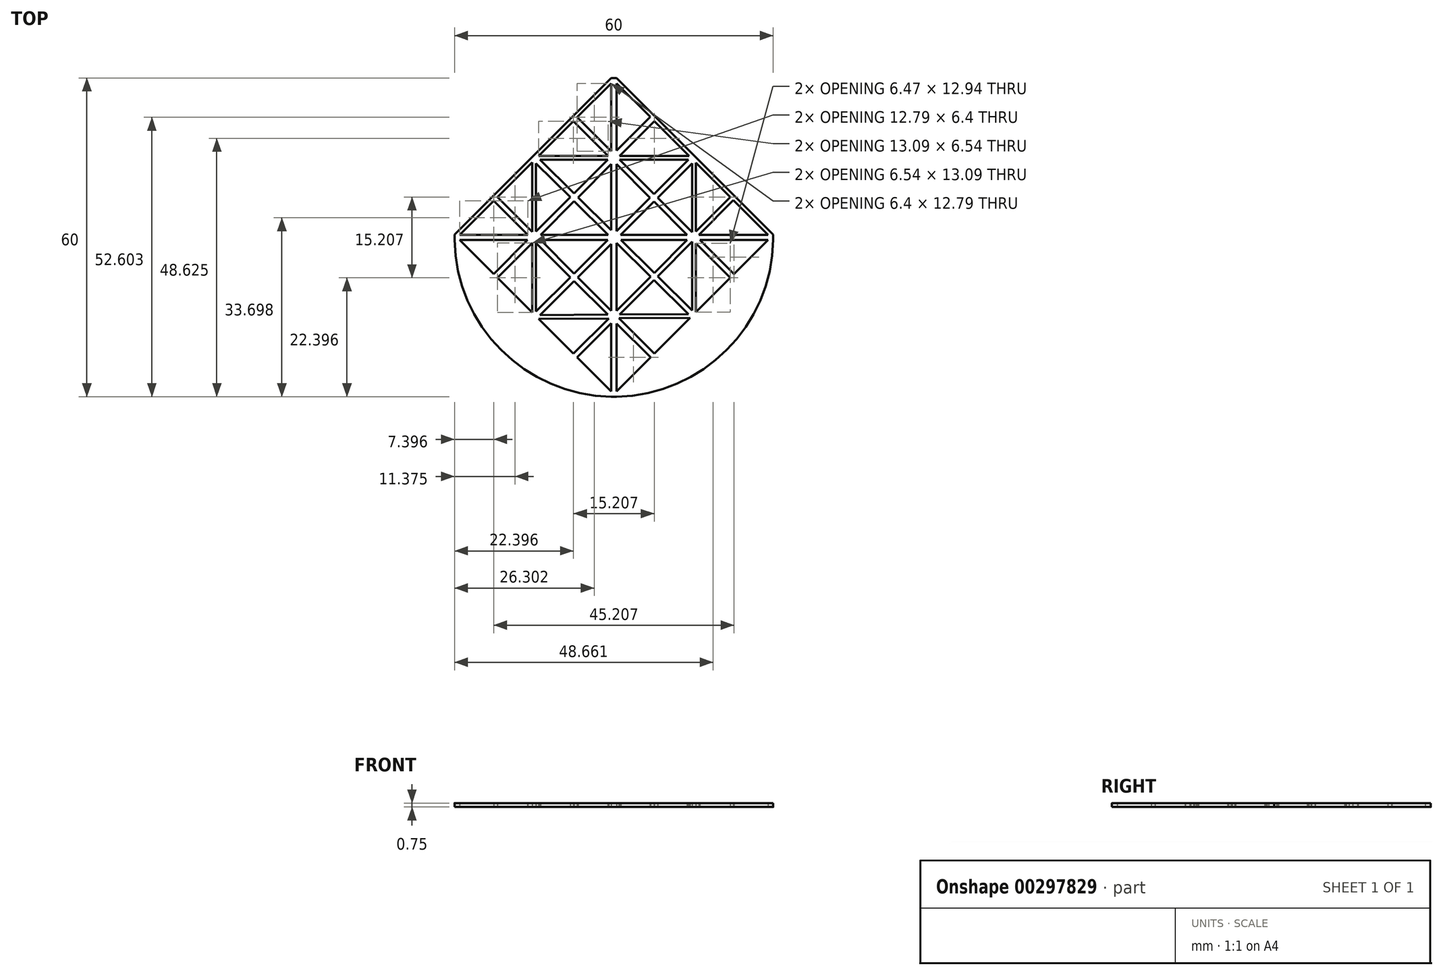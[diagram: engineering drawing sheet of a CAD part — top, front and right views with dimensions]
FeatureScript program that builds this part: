
annotation { "Feature Type Name" : "Feature", "Feature Type Description" : "" }
export const myFeature = defineFeature(function(context is Context, id is Id, definition is map)
    precondition{}
    {
        {
            var Q0;
            Q0=qCreatedBy(makeId("Top.planeOp"),FACE);
            var sketch = newSketch(context, id + "F0", { "sketchPlane" : qUnion([Q0])});
            skCircle(sketch, "E0", {"center": v(0, 0) * mm, "radius": 30 * mm});
            skLineSegment(sketch, "E1", {"start": v(-30, 0.5) * mm, "end": v(-0.5, 30) * mm});
            skLineSegment(sketch, "E2", {"start": v(0.5, 30) * mm, "end": v(30, 0.5) * mm});
            skLineSegment(sketch, "E3", {"start": v(30, 0.5) * mm, "end": v(30, -0.5) * mm});
            skLineSegment(sketch, "E4", {"start": v(-30, 0.5) * mm, "end": v(-30, 0.5) * mm});
            skLineSegment(sketch, "E5", {"start": v(-30, -0.5) * mm, "end": v(-0.5, -30) * mm});
            skLineSegment(sketch, "E6", {"start": v(0.5, -30) * mm, "end": v(30, -0.5) * mm});
            skLineSegment(sketch, "E7", {"start": v(30, 0.5) * mm, "end": v(30, 0.5) * mm});
            skLineSegment(sketch, "E8", {"start": v(30, -0.5) * mm, "end": v(30, -0.5) * mm});
            skLineSegment(sketch, "E9", {"start": v(0.5, 30) * mm, "end": v(0.5, 30) * mm});
            skLineSegment(sketch, "E10", {"start": v(-15.35, -14.15) * mm, "end": v(-15.35, -1.06) * mm});
            skLineSegment(sketch, "E11", {"start": v(-14.15, 15.35) * mm, "end": v(-1.06, 15.35) * mm});
            skLineSegment(sketch, "E12", {"start": v(15.43, 14.07) * mm, "end": v(15.43, 1.13) * mm});
            skLineSegment(sketch, "E13", {"start": v(14.36, -15.14) * mm, "end": v(0.95, -15.24) * mm});
            skLineSegment(sketch, "E14", {"start": v(-0.5, 30) * mm, "end": v(-0.5, 30) * mm});
            skLineSegment(sketch, "E15", {"start": v(-14.65, -13.94) * mm, "end": v(-8.2, -7.5) * mm});
            skLineSegment(sketch, "E16", {"start": v(14.72, -13.73) * mm, "end": v(8.24, -7.32) * mm});
            skLineSegment(sketch, "E17", {"start": v(-14.65, 13.95) * mm, "end": v(-8.2, 7.57) * mm});
            skLineSegment(sketch, "E18", {"start": v(7.6, 21.9) * mm, "end": v(1.06, 15.35) * mm});
            skLineSegment(sketch, "E19", {"start": v(-22.6, -6.9) * mm, "end": v(-16.24, -0.5) * mm});
            skLineSegment(sketch, "E20", {"start": v(22.46, 7.04) * mm, "end": v(15.99, 0.5) * mm});
            skLineSegment(sketch, "E21", {"start": v(-7.6, -21.9) * mm, "end": v(-0.96, -15.25) * mm});
            skLineSegment(sketch, "E22", {"start": v(7.6, -21.9) * mm, "end": v(0.95, -15.24) * mm});
            skLineSegment(sketch, "E23", {"start": v(-22.6, 6.9) * mm, "end": v(-16.2, 0.5) * mm});
            skLineSegment(sketch, "E24", {"start": v(22.78, -7.07) * mm, "end": v(16.2, -0.5) * mm});
            skLineSegment(sketch, "E25", {"start": v(-7.6, 21.9) * mm, "end": v(-1.06, 15.35) * mm});
            skLineSegment(sketch, "E26.trimOffspring", {"start": v(-15.35, 14.15) * mm, "end": v(-21.9, 7.6) * mm});
            skLineSegment(sketch, "E27.trimOffspring", {"start": v(-14.65, 13.95) * mm, "end": v(-14.65, 1.1) * mm});
            skLineSegment(sketch, "E28.trimOffspring", {"start": v(-7.6, 21.9) * mm, "end": v(-14.15, 15.35) * mm});
            skLineSegment(sketch, "E29.trimOffspring", {"start": v(-0.5, 29) * mm, "end": v(-0.5, 16.2) * mm});
            skLineSegment(sketch, "E30.trimOffspring", {"start": v(-0.5, 29) * mm, "end": v(-6.9, 22.6) * mm});
            skLineSegment(sketch, "E31.trimOffspring", {"start": v(0.5, 29) * mm, "end": v(0.5, 16.32) * mm});
            skLineSegment(sketch, "E32.trimOffspring", {"start": v(6.83, 22.67) * mm, "end": v(0.5, 29) * mm});
            skLineSegment(sketch, "E33.trimOffspring", {"start": v(0.5, 16.32) * mm, "end": v(6.83, 22.67) * mm});
            skLineSegment(sketch, "E34.trimOffspring", {"start": v(-0.5, 16.2) * mm, "end": v(-6.9, 22.6) * mm});
            skLineSegment(sketch, "E35.trimOffspring", {"start": v(-1.16, 14.65) * mm, "end": v(-13.93, 14.65) * mm});
            skLineSegment(sketch, "E36.trimOffspring", {"start": v(-0.5, 13.8) * mm, "end": v(-0.5, 1.34) * mm});
            skLineSegment(sketch, "E37.trimOffspring", {"start": v(0.5, 13.8) * mm, "end": v(6.82, 7.47) * mm});
            skLineSegment(sketch, "E38.trimOffspring", {"start": v(-0.5, 13.8) * mm, "end": v(-6.76, 7.54) * mm});
            skLineSegment(sketch, "E39.trimOffspring", {"start": v(-22.6, 6.9) * mm, "end": v(-29, 0.5) * mm});
            skLineSegment(sketch, "E40.trimOffspring", {"start": v(-29, -0.5) * mm, "end": v(-22.6, -6.9) * mm});
            skLineSegment(sketch, "E41.trimOffspring", {"start": v(-30, -0.5) * mm, "end": v(-30, -0.5) * mm});
            skLineSegment(sketch, "E42.trimOffspring", {"start": v(-29, 0.5) * mm, "end": v(-16.2, 0.5) * mm});
            skLineSegment(sketch, "E43.trimOffspring", {"start": v(-21.9, -7.6) * mm, "end": v(-15.35, -14.15) * mm});
            skLineSegment(sketch, "E44.trimOffspring", {"start": v(-14.15, -15.35) * mm, "end": v(-7.6, -21.9) * mm});
            skLineSegment(sketch, "E45.trimOffspring", {"start": v(-13.93, -14.64) * mm, "end": v(-1.16, -14.55) * mm});
            skLineSegment(sketch, "E46.trimOffspring", {"start": v(-6.9, -22.6) * mm, "end": v(-0.5, -29) * mm});
            skLineSegment(sketch, "E47.trimOffspring", {"start": v(-0.5, -30) * mm, "end": v(-0.5, -30) * mm});
            skLineSegment(sketch, "E48.trimOffspring", {"start": v(0.5, -30) * mm, "end": v(0.5, -30) * mm});
            skLineSegment(sketch, "E49.trimOffspring", {"start": v(6.9, -22.6) * mm, "end": v(0.5, -29) * mm});
            skLineSegment(sketch, "E50.trimOffspring", {"start": v(14.72, -13.73) * mm, "end": v(14.72, -0.78) * mm});
            skLineSegment(sketch, "E51.trimOffspring", {"start": v(14.36, -15.14) * mm, "end": v(7.6, -21.9) * mm});
            skLineSegment(sketch, "E52.trimOffspring", {"start": v(-7.46, 6.83) * mm, "end": v(-1.07, 0.5) * mm});
            skLineSegment(sketch, "E53.trimOffspring", {"start": v(-7.5, 8.28) * mm, "end": v(-1.16, 14.65) * mm});
            skLineSegment(sketch, "E54.trimOffspring", {"start": v(-7.5, 8.28) * mm, "end": v(-13.93, 14.65) * mm});
            skLineSegment(sketch, "E55.trimOffspring", {"start": v(-7.46, 6.83) * mm, "end": v(-13.8, 0.5) * mm});
            skLineSegment(sketch, "E56.trimOffspring", {"start": v(-1.17, -0.5) * mm, "end": v(-13.8, -0.5) * mm});
            skLineSegment(sketch, "E57.trimOffspring", {"start": v(-0.5, -1.24) * mm, "end": v(-0.5, -13.8) * mm});
            skLineSegment(sketch, "E58.trimOffspring", {"start": v(-0.5, 1.34) * mm, "end": v(-6.76, 7.54) * mm});
            skLineSegment(sketch, "E59.trimOffspring", {"start": v(0.5, 1.17) * mm, "end": v(6.82, 7.47) * mm});
            skLineSegment(sketch, "E60.trimOffspring", {"start": v(1.24, 0.5) * mm, "end": v(13.8, 0.5) * mm});
            skLineSegment(sketch, "E61.trimOffspring", {"start": v(0.5, -1.06) * mm, "end": v(0.5, -13.8) * mm});
            skLineSegment(sketch, "E62.trimOffspring", {"start": v(-0.5, -1.24) * mm, "end": v(-6.78, -7.5) * mm});
            skLineSegment(sketch, "E63.trimOffspring", {"start": v(0.5, -1.06) * mm, "end": v(6.9, -7.4) * mm});
            skLineSegment(sketch, "E64.trimOffspring", {"start": v(1.06, 15.35) * mm, "end": v(14.15, 15.35) * mm});
            skLineSegment(sketch, "E65.trimOffspring", {"start": v(7.53, 8.18) * mm, "end": v(14, 14.65) * mm});
            skLineSegment(sketch, "E66.trimOffspring", {"start": v(7.53, 6.77) * mm, "end": v(1.24, 0.5) * mm});
            skLineSegment(sketch, "E67.trimOffspring", {"start": v(7.53, 6.77) * mm, "end": v(13.8, 0.5) * mm});
            skLineSegment(sketch, "E68.trimOffspring", {"start": v(14.15, 15.35) * mm, "end": v(7.6, 21.9) * mm});
            skLineSegment(sketch, "E69.trimOffspring", {"start": v(14, 14.65) * mm, "end": v(1.06, 14.65) * mm});
            skLineSegment(sketch, "E70.trimOffspring", {"start": v(14.72, 13.94) * mm, "end": v(8.23, 7.47) * mm});
            skLineSegment(sketch, "E71.trimOffspring", {"start": v(21.9, 7.6) * mm, "end": v(15.43, 14.07) * mm});
            skLineSegment(sketch, "E72.trimOffspring", {"start": v(29, 0.5) * mm, "end": v(22.46, 7.04) * mm});
            skLineSegment(sketch, "E73.trimOffspring", {"start": v(29, -0.5) * mm, "end": v(15.43, -14.07) * mm});
            skLineSegment(sketch, "E74.trimOffspring", {"start": v(29, -0.5) * mm, "end": v(16.2, -0.5) * mm});
            skLineSegment(sketch, "E75.trimOffspring", {"start": v(14.72, 1) * mm, "end": v(14.72, 13.94) * mm});
            skLineSegment(sketch, "E76.trimOffspring", {"start": v(14.72, 1) * mm, "end": v(1.06, 14.65) * mm});
            skLineSegment(sketch, "E77.trimOffspring", {"start": v(15.43, 1.13) * mm, "end": v(21.9, 7.6) * mm});
            skLineSegment(sketch, "E78.trimOffspring", {"start": v(14.72, -0.78) * mm, "end": v(8.24, -7.32) * mm});
            skLineSegment(sketch, "E79.trimOffspring", {"start": v(15.43, -1.13) * mm, "end": v(22.07, -7.78) * mm});
            skLineSegment(sketch, "E80.trimOffspring", {"start": v(15.43, -1.13) * mm, "end": v(15.43, -14.07) * mm});
            skLineSegment(sketch, "E81.trimOffspring", {"start": v(15.99, 0.5) * mm, "end": v(29, 0.5) * mm});
            skLineSegment(sketch, "E82.trimOffspring", {"start": v(13.8, -0.5) * mm, "end": v(1.36, -0.5) * mm});
            skLineSegment(sketch, "E83.trimOffspring", {"start": v(-0.96, -15.25) * mm, "end": v(-14.15, -15.35) * mm});
            skLineSegment(sketch, "E84.trimOffspring", {"start": v(-0.5, -16.14) * mm, "end": v(-0.5, -29) * mm});
            skLineSegment(sketch, "E85.trimOffspring", {"start": v(-0.5, -16.14) * mm, "end": v(-6.9, -22.6) * mm});
            skLineSegment(sketch, "E86.trimOffspring", {"start": v(0.5, -16.2) * mm, "end": v(6.9, -22.6) * mm});
            skLineSegment(sketch, "E87.trimOffspring", {"start": v(0.5, -16.2) * mm, "end": v(0.5, -29) * mm});
            skLineSegment(sketch, "E88.trimOffspring", {"start": v(1.1, -14.53) * mm, "end": v(14.01, -14.44) * mm});
            skLineSegment(sketch, "E89.trimOffspring", {"start": v(0.5, -13.8) * mm, "end": v(6.9, -7.4) * mm});
            skLineSegment(sketch, "E90.trimOffspring", {"start": v(-0.5, -13.8) * mm, "end": v(-6.78, -7.5) * mm});
            skLineSegment(sketch, "E91.trimOffspring", {"start": v(-7.5, -6.8) * mm, "end": v(-13.8, -0.5) * mm});
            skLineSegment(sketch, "E92.trimOffspring", {"start": v(-7.5, -6.8) * mm, "end": v(-1.17, -0.5) * mm});
            skLineSegment(sketch, "E93.trimOffspring", {"start": v(-7.5, -8.22) * mm, "end": v(-1.16, -14.55) * mm});
            skLineSegment(sketch, "E94.trimOffspring", {"start": v(-7.5, -8.22) * mm, "end": v(-13.93, -14.64) * mm});
            skLineSegment(sketch, "E95.trimOffspring", {"start": v(-16.24, -0.5) * mm, "end": v(-29, -0.5) * mm});
            skLineSegment(sketch, "E96.trimOffspring", {"start": v(-15.35, -1.06) * mm, "end": v(-21.9, -7.6) * mm});
            skLineSegment(sketch, "E97.trimOffspring", {"start": v(-14.65, -1.06) * mm, "end": v(-14.65, -13.94) * mm});
            skLineSegment(sketch, "E98.trimOffspring", {"start": v(-13.8, 0.5) * mm, "end": v(-1.07, 0.5) * mm});
            skLineSegment(sketch, "E99.trimOffspring", {"start": v(-14.65, 1.1) * mm, "end": v(-8.2, 7.57) * mm});
            skLineSegment(sketch, "E100.trimOffspring", {"start": v(-15.35, 1.06) * mm, "end": v(-21.9, 7.6) * mm});
            skLineSegment(sketch, "E101.trimOffspring", {"start": v(-15.35, 1.06) * mm, "end": v(-15.35, 14.15) * mm});
            skLineSegment(sketch, "E102.trimOffspring", {"start": v(-14.65, -1.06) * mm, "end": v(-8.2, -7.5) * mm});
            skLineSegment(sketch, "E103", {"start": v(0.5, 13.8) * mm, "end": v(0.5, 1.17) * mm});
            skLineSegment(sketch, "E104.trimOffspring", {"start": v(7.6, -6.69) * mm, "end": v(13.8, -0.5) * mm});
            skLineSegment(sketch, "E105.trimOffspring", {"start": v(7.6, -6.69) * mm, "end": v(1.36, -0.5) * mm});
            skLineSegment(sketch, "E106.trimOffspring", {"start": v(7.54, -8.03) * mm, "end": v(1.1, -14.53) * mm});
            skLineSegment(sketch, "E107.trimOffspring", {"start": v(7.54, -8.03) * mm, "end": v(14.01, -14.44) * mm});
            skSolve(sketch);
        }
        {
            var Q0;
            Q0=makeQuery(id+"F0.imprint","IMPRINT",FACE,{"disambiguationData":[TD([[makeQuery(id+"F0.imprint","IMPRINT",EDGE,{"derivedFrom":sQuery(id+"F0.wireOp",EDGE,"E10")}),-1.0]])]});
            extrude(context, id + "F1", {"entities" : qUnion([Q0]), "depth" : 0.5 * mm});
        }
        {
            var Q0;
            {var subQ0=sQuery(id+"F0.wireOp",EDGE,"E6");var subQ1=sQuery(id+"F0.wireOp",EDGE,"E0");var subQ2=makeQuery(id+"F0.imprint","INTERSECT",VERTEX,{"disambiguationData":[OD(0.0)],"derivedFrom":[subQ1,subQ0]});Q0=makeQuery(id+"F0.imprint","IMPRINT",FACE,{"disambiguationData":[TD([[makeQuery(id+"F0.imprint","IMPRINT",EDGE,{"disambiguationData":[TD([[subQ2,-1.0]])],"derivedFrom":subQ1}),1.0]])]});}
            var Q1;
            {var subQ0=sQuery(id+"F0.wireOp",EDGE,"E2");var subQ1=sQuery(id+"F0.wireOp",EDGE,"E0");var subQ2=makeQuery(id+"F0.imprint","INTERSECT",VERTEX,{"disambiguationData":[OD(0.0)],"derivedFrom":[subQ1,subQ0]});Q1=makeQuery(id+"F0.imprint","IMPRINT",FACE,{"disambiguationData":[TD([[makeQuery(id+"F0.imprint","IMPRINT",EDGE,{"disambiguationData":[TD([[subQ2,-1.0]])],"derivedFrom":subQ1}),1.0]])]});}
            var Q2;
            {var subQ0=sQuery(id+"F0.wireOp",EDGE,"E1");var subQ1=sQuery(id+"F0.wireOp",EDGE,"E0");var subQ2=makeQuery(id+"F0.imprint","INTERSECT",VERTEX,{"disambiguationData":[OD(0.0)],"derivedFrom":[subQ1,subQ0]});Q2=makeQuery(id+"F0.imprint","IMPRINT",FACE,{"disambiguationData":[TD([[makeQuery(id+"F0.imprint","IMPRINT",EDGE,{"disambiguationData":[TD([[subQ2,-1.0]])],"derivedFrom":subQ1}),1.0]])]});}
            var Q3;
            {var subQ0=sQuery(id+"F0.wireOp",EDGE,"E5");var subQ1=sQuery(id+"F0.wireOp",EDGE,"E0");var subQ2=makeQuery(id+"F0.imprint","INTERSECT",VERTEX,{"disambiguationData":[OD(0.0)],"derivedFrom":[subQ1,subQ0]});Q3=makeQuery(id+"F0.imprint","IMPRINT",FACE,{"disambiguationData":[TD([[makeQuery(id+"F0.imprint","IMPRINT",EDGE,{"disambiguationData":[TD([[subQ2,-1.0]])],"derivedFrom":subQ1}),1.0]])]});}
            extrude(context, id + "F2", {"entities" : qUnion([Q0, Q1, Q2, Q3]), "operationType" : NewBodyOperationType.ADD, "depth" : 0.75 * mm});
        }
    });
